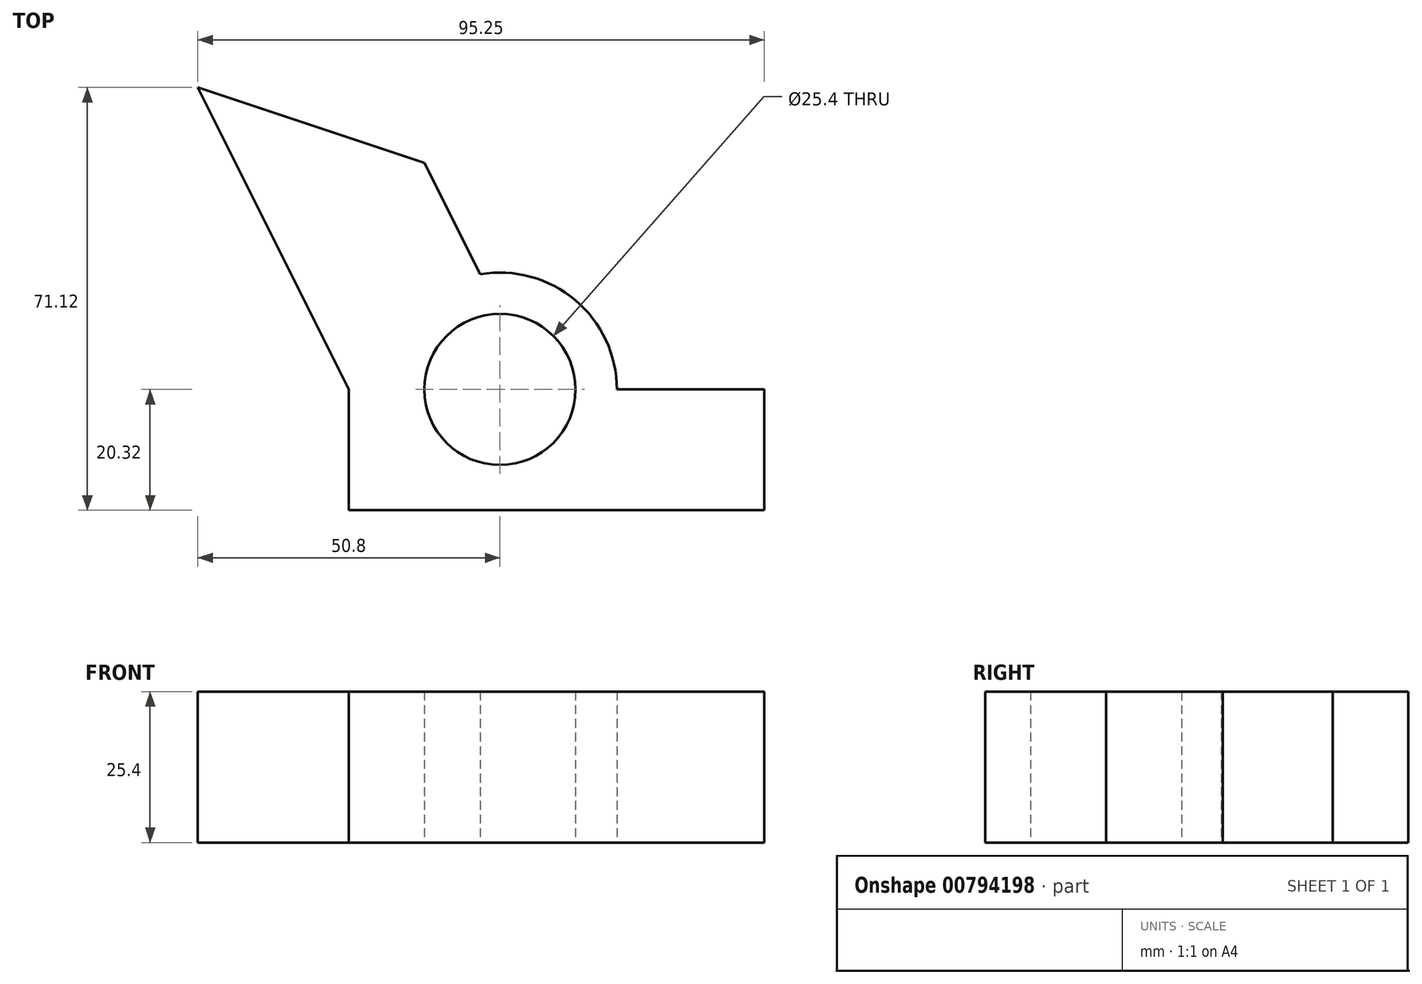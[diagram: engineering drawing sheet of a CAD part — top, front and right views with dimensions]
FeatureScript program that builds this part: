
annotation { "Feature Type Name" : "Feature", "Feature Type Description" : "" }
export const myFeature = defineFeature(function(context is Context, id is Id, definition is map)
    precondition{}
    {
        {
            var Q0;
            Q0=qCreatedBy(makeId("Top.planeOp"),FACE);
            var sketch = newSketch(context, id + "F0", { "sketchPlane" : qUnion([Q0])});
            skCircle(sketch, "E0", {"center": v(0, 0) * mm, "radius": 12.7 * mm});
            skLineSegment(sketch, "E1", {"start": v(-12.7, 0) * mm, "end": v(-25.4, 0) * mm});
            skLineSegment(sketch, "E2", {"start": v(-25.4, 0) * mm, "end": v(-25.4, -20.32) * mm});
            skLineSegment(sketch, "E3", {"start": v(-25.4, -20.32) * mm, "end": v(44.45, -20.32) * mm});
            skLineSegment(sketch, "E4", {"start": v(44.45, -20.32) * mm, "end": v(44.45, 0) * mm});
            skLineSegment(sketch, "E5", {"start": v(44.45, 0) * mm, "end": v(12.7, 0) * mm});
            skPoint(sketch, "E6", {"position": v(0, 12.7) * mm});
            skPoint(sketch, "E7", {"position": v(-12.7, 0) * mm});
            skPoint(sketch, "E8", {"position": v(-25.4, 0) * mm});
            skPoint(sketch, "E9", {"position": v(-25.4, 12.7) * mm});
            skPoint(sketch, "E10", {"position": v(-12.7, 12.7) * mm});
            skPoint(sketch, "E11", {"position": v(0, 25.4) * mm});
            skPoint(sketch, "E12", {"position": v(-12.7, 25.4) * mm});
            skPoint(sketch, "E13", {"position": v(-25.4, 25.4) * mm});
            skPoint(sketch, "E14", {"position": v(-38.1, 0) * mm});
            skPoint(sketch, "E15", {"position": v(-38.1, 12.7) * mm});
            skPoint(sketch, "E16", {"position": v(-38.1, 25.4) * mm});
            skPoint(sketch, "E17", {"position": v(-38.1, 38.1) * mm});
            skPoint(sketch, "E18", {"position": v(-25.4, 38.1) * mm});
            skPoint(sketch, "E19", {"position": v(-12.7, 38.1) * mm});
            skPoint(sketch, "E20", {"position": v(0, 38.1) * mm});
            skPoint(sketch, "E21", {"position": v(0, 50.8) * mm});
            skPoint(sketch, "E22", {"position": v(-12.7, 50.8) * mm});
            skPoint(sketch, "E23", {"position": v(-25.4, 50.8) * mm});
            skPoint(sketch, "E24", {"position": v(-38.1, 50.8) * mm});
            skPoint(sketch, "E25", {"position": v(-50.8, 50.8) * mm});
            skPoint(sketch, "E26", {"position": v(-50.8, 38.1) * mm});
            skPoint(sketch, "E27", {"position": v(-50.8, 25.4) * mm});
            skPoint(sketch, "E28", {"position": v(-50.8, 12.7) * mm});
            skPoint(sketch, "E29", {"position": v(-50.8, 0) * mm});
            skLineSegment(sketch, "E30", {"start": v(0, 12.7) * mm, "end": v(-12.7, 38.1) * mm});
            skLineSegment(sketch, "E31", {"start": v(-12.7, 38.1) * mm, "end": v(-50.8, 50.8) * mm});
            skLineSegment(sketch, "E32", {"start": v(-50.8, 50.8) * mm, "end": v(-38.1, 25.4) * mm});
            skLineSegment(sketch, "E33", {"start": v(-38.1, 25.4) * mm, "end": v(-25.4, 0) * mm});
            skCircle(sketch, "E34", {"center": v(0, 0) * mm, "radius": 19.66 * mm});
            skSolve(sketch);
        }
        {
            var Q0;
            {var subQ0=sQuery(id+"F0.wireOp",EDGE,"E31");Q0=makeQuery(id+"F0.imprint","IMPRINT",FACE,{"disambiguationData":[TD([[makeQuery(id+"F0.imprint","IMPRINT",EDGE,{"derivedFrom":subQ0}),1.0]])]});}
            var Q1;
            {var subQ0=sQuery(id+"F0.wireOp",EDGE,"E1");var subQ1=sQuery(id+"F0.wireOp",EDGE,"E0");var subQ2=makeQuery(id+"F0.imprint","INTERSECT",VERTEX,{"derivedFrom":[subQ1,subQ0]});Q1=makeQuery(id+"F0.imprint","IMPRINT",FACE,{"disambiguationData":[TD([[makeQuery(id+"F0.imprint","IMPRINT",EDGE,{"disambiguationData":[TD([[subQ2,1.0]])],"derivedFrom":subQ1}),-1.0]])]});}
            var Q2;
            {var subQ0=sQuery(id+"F0.wireOp",EDGE,"E5");var subQ1=sQuery(id+"F0.wireOp",EDGE,"E0");var subQ2=makeQuery(id+"F0.imprint","INTERSECT",VERTEX,{"derivedFrom":[subQ1,subQ0]});Q2=makeQuery(id+"F0.imprint","IMPRINT",FACE,{"disambiguationData":[TD([[makeQuery(id+"F0.imprint","IMPRINT",EDGE,{"disambiguationData":[TD([[subQ2,-1.0]])],"derivedFrom":subQ1}),-1.0]])]});}
            var Q3;
            {var subQ0=sQuery(id+"F0.wireOp",EDGE,"E1");var subQ1=sQuery(id+"F0.wireOp",EDGE,"E0");var subQ2=makeQuery(id+"F0.imprint","INTERSECT",VERTEX,{"derivedFrom":[subQ1,subQ0]});Q3=makeQuery(id+"F0.imprint","IMPRINT",FACE,{"disambiguationData":[TD([[makeQuery(id+"F0.imprint","IMPRINT",EDGE,{"disambiguationData":[TD([[subQ2,-1.0]])],"derivedFrom":subQ1}),-1.0]])]});}
            var Q4;
            {var subQ6=sQuery(id+"F0.wireOp",EDGE,"E2");Q4=makeQuery(id+"F0.imprint","IMPRINT",FACE,{"disambiguationData":[TD([[makeQuery(id+"F0.imprint","IMPRINT",EDGE,{"derivedFrom":subQ6}),1.0]])]});}
            extrude(context, id + "F1", {"entities" : qUnion([Q0, Q1, Q2, Q3, Q4]), "depth" : 25.4 * mm, "offsetDistance" : 25.4 * mm});
        }
    });
